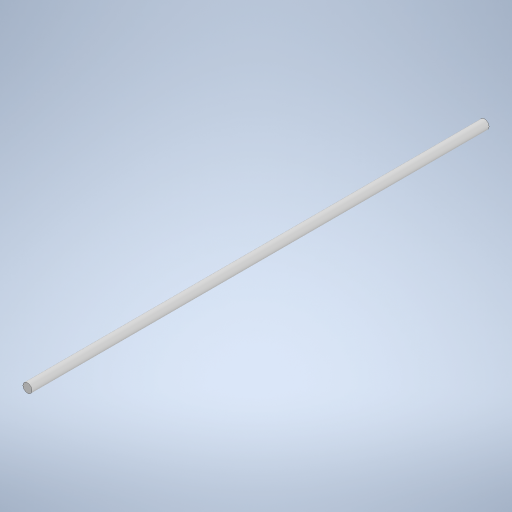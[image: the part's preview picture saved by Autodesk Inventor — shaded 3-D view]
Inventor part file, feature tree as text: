
AUTODESK INVENTOR PART (.ipt)
format: ipt  version: 2024 (Build 280153000, 153)  size: 235,008 bytes
history: native  units: mm
features: extrude x1, sketch x1
ambient origin geometry x8: Origin, YZ Plane, XZ Plane, XY Plane, X Axis, Y Axis, Z Axis, Center Point
bodies: Solid1 (feature_tree)
feature tree (2):
  extrude  "Extrusion1"  Depth=100.0mm TaperAngle=0.0deg
  sketch  "Sketch1"  dims[d0=2.0mm d1=100.0mm d2=0.0mm]
